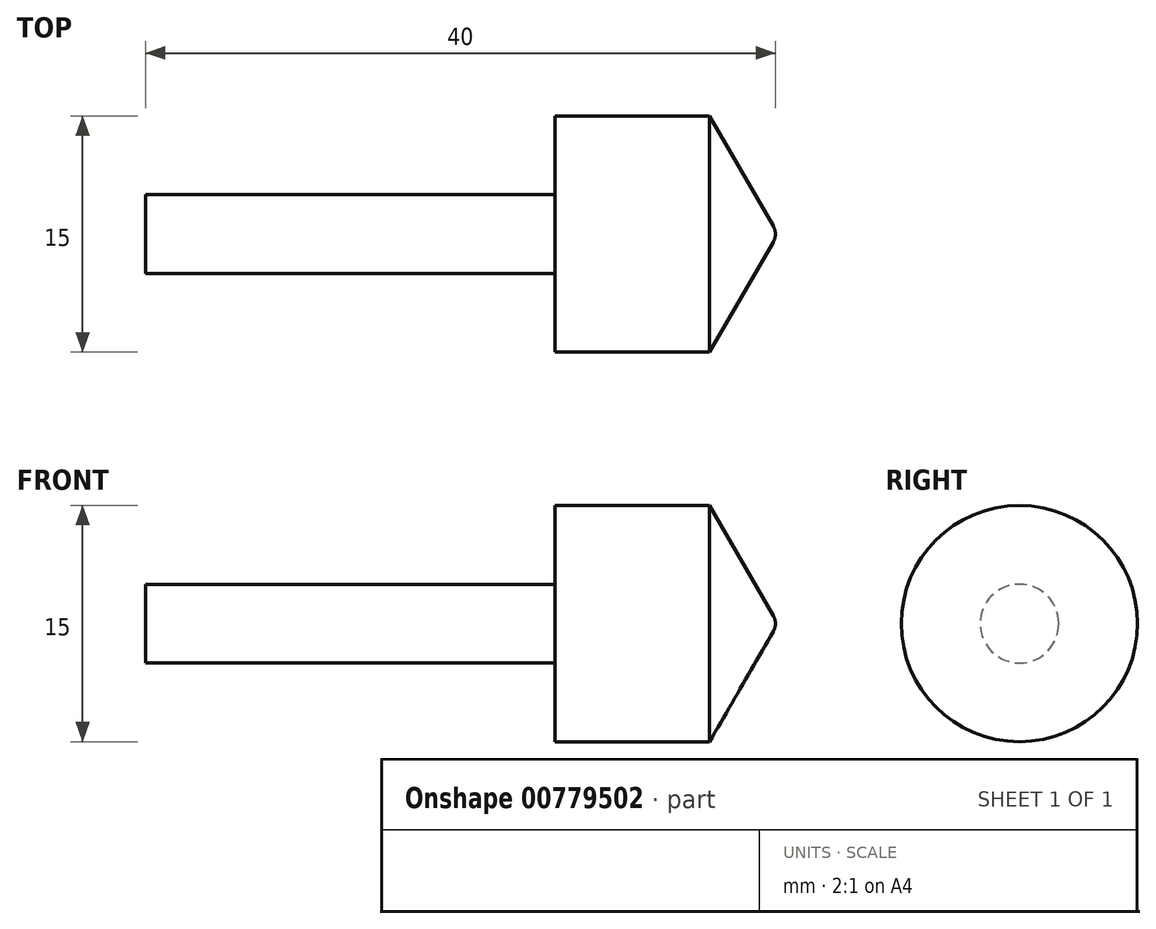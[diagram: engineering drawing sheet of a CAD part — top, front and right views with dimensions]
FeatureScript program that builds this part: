
annotation { "Feature Type Name" : "Feature", "Feature Type Description" : "" }
export const myFeature = defineFeature(function(context is Context, id is Id, definition is map)
    precondition{}
    {
        {
            var Q0;
            Q0=qCreatedBy(makeId("Front.planeOp"),FACE);
            var sketch = newSketch(context, id + "F0", { "sketchPlane" : qUnion([Q0])});
            skLineSegment(sketch, "E0", {"start": v(-26, 0) * mm, "end": v(-26, 2.5) * mm});
            skLineSegment(sketch, "E1", {"start": v(-26, 2.5) * mm, "end": v(0, 2.5) * mm});
            skLineSegment(sketch, "E2", {"start": v(0, 2.5) * mm, "end": v(0, 7.5) * mm});
            skLineSegment(sketch, "E3", {"start": v(0, 7.5) * mm, "end": v(9.82, 7.5) * mm});
            skLineSegment(sketch, "E4", {"start": v(9.82, 7.5) * mm, "end": v(13.87, 0.5) * mm});
            skLineSegment(sketch, "E5", {"start": v(14.15, 0) * mm, "end": v(-26, 0) * mm});
            skArc(sketch, "E6", {"start": v(14, 0) * mm, "mid": v(13.97, 0.26) * mm, "end": v(13.87, 0.5) * mm});
            skSolve(sketch);
        }
        {
            var Q0;
            Q0 = qSketchRegion(id + "F0", true);
            var Q1;
            Q1=sQuery(id+"F0.wireOp",EDGE,"E5");
            revolve(context, id + "F1", {"surfaceOperationType" : NewSurfaceOperationType.NEW, "entities" : qUnion([Q0]), "axis" : qUnion([Q1]), "revolveType" : RevolveType.FULL});
        }
    });
